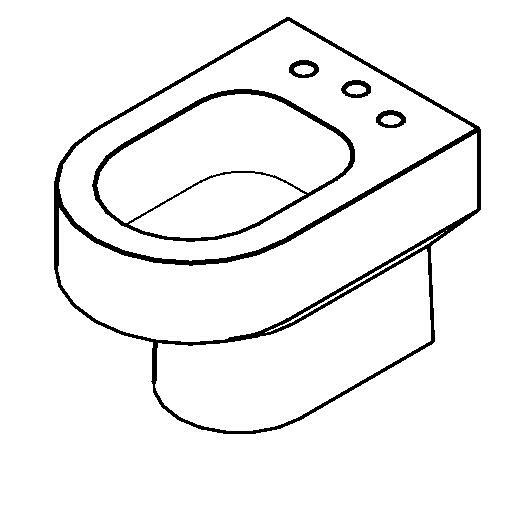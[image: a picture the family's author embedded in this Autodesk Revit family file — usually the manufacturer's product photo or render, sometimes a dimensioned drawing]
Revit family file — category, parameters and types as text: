
# Revit family: Deca_Bidê Carrara_B.60_3 Furos.3
name_source: partatom
category: Plumbing Fixtures
revit_build: Autodesk Revit Architecture 2012 (Build: 20120126_0600(x64)
units: mm (PartAtom-declared; Revit-internal decimal feet)

## types (3) — shared parameters
Acompanha o Produto = Não Aplicável
Aprovado por = Contino/quattroD
Atendimento ao Cliente = 0800-011-7073
Criador por = Contino/quattroD
Description = Bidê
Descrição = Bidê
Diâmetro Ponto de Esgoto = 40 mm  [stored 0.131234 ft]
Fabricante = Deca
Flow Pressure = 0.00 psi
Informações Complementares = 3 furos - utilizar com misturador
Linha = Carrara
Louça/Metais = Louça
Manufacturer = Deca
Material = Cerâmica (Vitreous China)
Norma = NBR15097-1 NBR15097-2
Peso Liquido (Kg) = 22.5
Produto = Bidê 3 furos linha Carrara
Raio Ponto de Esgoto = 20 mm  [stored 0.0656168 ft]
Segmento = Banheiro Luxo
URL = www.deca.com.br
Variações de COR = B.60.17 ,B.60.37, B.60.95
Vendido Separadamente = Parafusos de fixação (SP.13.01) e Válvula de escoamento (1601.C/1602. C/1602.C.PLA)
zero-valued in all types: CWFU, Default Elevation, WFU

## per-type parameters (varying)
| type | Bidê | Código | Model |
| B.60.17 - Branco GE17 | Deca GE17 Branco Gelo Cerâmica | B.60.17 | B.60.17 |
| B.60.37 - Creme CR37 | Deca CR37 Creme Cerâmica | B.60.37 | B.60.37 |
| B.60.95 - Ébano EB95 | Deca EB95 Ébano Cerâmica | B.60.95 | B.60.95 |

note: [stored X ft] marks values corroborated as IEEE doubles in the binary element streams (Revit-internal decimal feet)

## geometry (parser evidence)
native form markers: Blend x6, Sweep x1
no freeform markers — native parametric forms only
